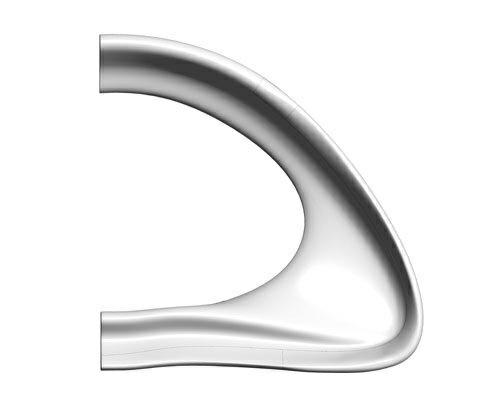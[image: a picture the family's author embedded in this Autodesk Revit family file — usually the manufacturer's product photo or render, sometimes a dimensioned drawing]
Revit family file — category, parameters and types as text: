
# Revit family: CITY ALPHABET letter „V” horizontal_1
name_source: partatom
category: Furniture
revit_build: Autodesk Revit 2018 (Build: 20190510_1515(x64)
units: mm (PartAtom-declared; Revit-internal decimal feet)

## family parameters
Cut with Voids When Loaded = No
Host = Face
OmniClass Number = 23.40.10.11.14
OmniClass Title = Exterior Seating
Room Calculation Point = No
Shared = No

## types (1)
- CITY ALPHABET letter „V”
    Default Elevation = 1219 mm
    Height = 850 mm  [stored 2.78871 ft]
    IfcExportAs = IfcFurnishingElement
    Length = 1850 mm  [stored 6.06955 ft]
    Manufacturer = Astrini Design
    Material information = Colour choice from RAL colour standard. Customer may inquire about specific request regarding individual order.
    Model = CITY ALPHABET letter „V”
    Operating temperature = -40°C to 80°C, ( -40°F to 176°F )
    Type Comments = Bench
    Type Image = V.jpg
    URL = https://astrini-design.pl
    Weight (approximately) = 80.00 kg
    Weight - filled (approximately) = 130.00 kg
    Width = 1900 mm  [stored 6.2336 ft]

note: [stored X ft] marks values corroborated as IEEE doubles in the binary element streams (Revit-internal decimal feet)
